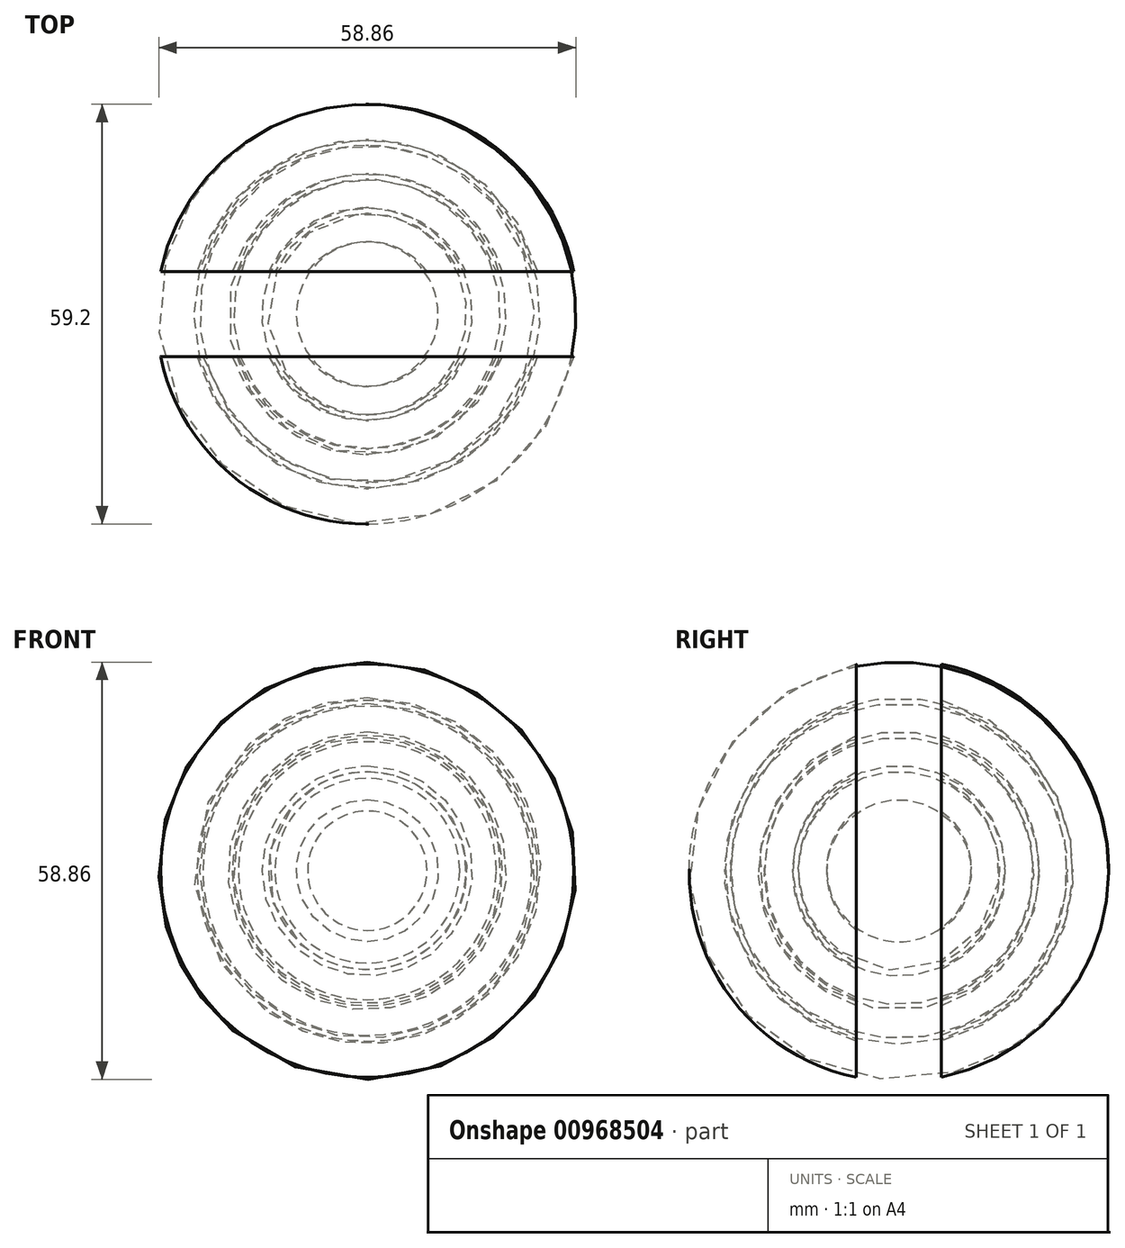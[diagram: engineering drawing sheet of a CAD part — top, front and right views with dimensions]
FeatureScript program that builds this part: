
annotation { "Feature Type Name" : "Feature", "Feature Type Description" : "" }
export const myFeature = defineFeature(function(context is Context, id is Id, definition is map)
    precondition{}
    {
        {
            var Q0;
            Q0=qCreatedBy(makeId("Top.planeOp"),FACE);
            var sketch = newSketch(context, id + "F0", { "sketchPlane" : qUnion([Q0])});
            skArc(sketch, "E0", {"start": v(-13.75, 6) * mm, "mid": v(-15, 0) * mm, "end": v(-13.75, -6) * mm});
            skArc(sketch, "E1.0", {"start": v(-18.03, 6) * mm, "mid": v(-19, 0) * mm, "end": v(-18.03, -6) * mm});
            skArc(sketch, "E2.0", {"start": v(-18.87, 6) * mm, "mid": v(-19.8, 0) * mm, "end": v(-18.87, -6) * mm});
            skArc(sketch, "E3.0", {"start": v(-23.03, 6) * mm, "mid": v(-23.8, 0) * mm, "end": v(-23.03, -6) * mm});
            skArc(sketch, "E4.0", {"start": v(-23.86, 6) * mm, "mid": v(-24.6, 0) * mm, "end": v(-23.86, -6) * mm});
            skArc(sketch, "E5.0", {"start": v(-28.99, 6) * mm, "mid": v(-29.6, 0) * mm, "end": v(-28.99, -6) * mm});
            skLineSegment(sketch, "E6", {"start": v(-28.99, 6) * mm, "end": v(-23.86, 6) * mm});
            skLineSegment(sketch, "E7.MirrorCS", {"start": v(-28.99, -6) * mm, "end": v(-23.86, -6) * mm});
            skArc(sketch, "E8.0", {"start": v(-12.87, 6) * mm, "mid": v(-14.2, 0) * mm, "end": v(-12.87, -6) * mm});
            skArc(sketch, "E9.0", {"start": v(-8.25, 6) * mm, "mid": v(-10.2, 0) * mm, "end": v(-8.25, -6) * mm});
            skPoint(sketch, "E10.trimOffspring.end.orphan", {"position": v(29.33, 4) * mm});
            skLineSegment(sketch, "E11", {"start": v(0.17, -5) * mm, "end": v(0.17, 6) * mm});
            skPoint(sketch, "E12.orphan", {"position": v(29.33, -4) * mm});
            skLineSegment(sketch, "E13.trimOffspring", {"start": v(-12.87, -6) * mm, "end": v(-8.25, -6) * mm});
            skLineSegment(sketch, "E14.trimOffspring", {"start": v(-18.03, -6) * mm, "end": v(-13.75, -6) * mm});
            skLineSegment(sketch, "E15.trimOffspring", {"start": v(-23.03, -6) * mm, "end": v(-18.87, -6) * mm});
            skLineSegment(sketch, "E16.trimOffspring", {"start": v(-18.03, 6) * mm, "end": v(-13.75, 6) * mm});
            skLineSegment(sketch, "E17.trimOffspring", {"start": v(-12.87, 6) * mm, "end": v(-8.25, 6) * mm});
            skLineSegment(sketch, "E18.trimOffspring", {"start": v(-23.03, 6) * mm, "end": v(-18.87, 6) * mm});
            skSolve(sketch);
        }
        {
            var Q0;
            Q0=makeQuery(id+"F0.imprint","IMPRINT",FACE,{"disambiguationData":[TD([[makeQuery(id+"F0.imprint","IMPRINT",EDGE,{"derivedFrom":sQuery(id+"F0.wireOp",EDGE,"E4.0")}),-1.0]])]});
            var Q1;
            Q1=makeQuery(id+"F0.imprint","IMPRINT",FACE,{"disambiguationData":[TD([[makeQuery(id+"F0.imprint","IMPRINT",EDGE,{"derivedFrom":sQuery(id+"F0.wireOp",EDGE,"E2.0")}),-1.0]])]});
            var Q2;
            Q2=makeQuery(id+"F0.imprint","IMPRINT",FACE,{"disambiguationData":[TD([[makeQuery(id+"F0.imprint","IMPRINT",EDGE,{"derivedFrom":sQuery(id+"F0.wireOp",EDGE,"E0")}),-1.0]])]});
            var Q3;
            Q3=makeQuery(id+"F0.imprint","IMPRINT",FACE,{"disambiguationData":[TD([[makeQuery(id+"F0.imprint","IMPRINT",EDGE,{"derivedFrom":sQuery(id+"F0.wireOp",EDGE,"E8.0")}),1.0]])]});
            var Q4;
            Q4=sQuery(id+"F0.wireOp",EDGE,"E11");
            revolve(context, id + "F1", {"surfaceOperationType" : NewSurfaceOperationType.NEW, "entities" : qUnion([Q0, Q1, Q2, Q3]), "axis" : qUnion([Q4]), "revolveType" : RevolveType.FULL});
        }
    });
